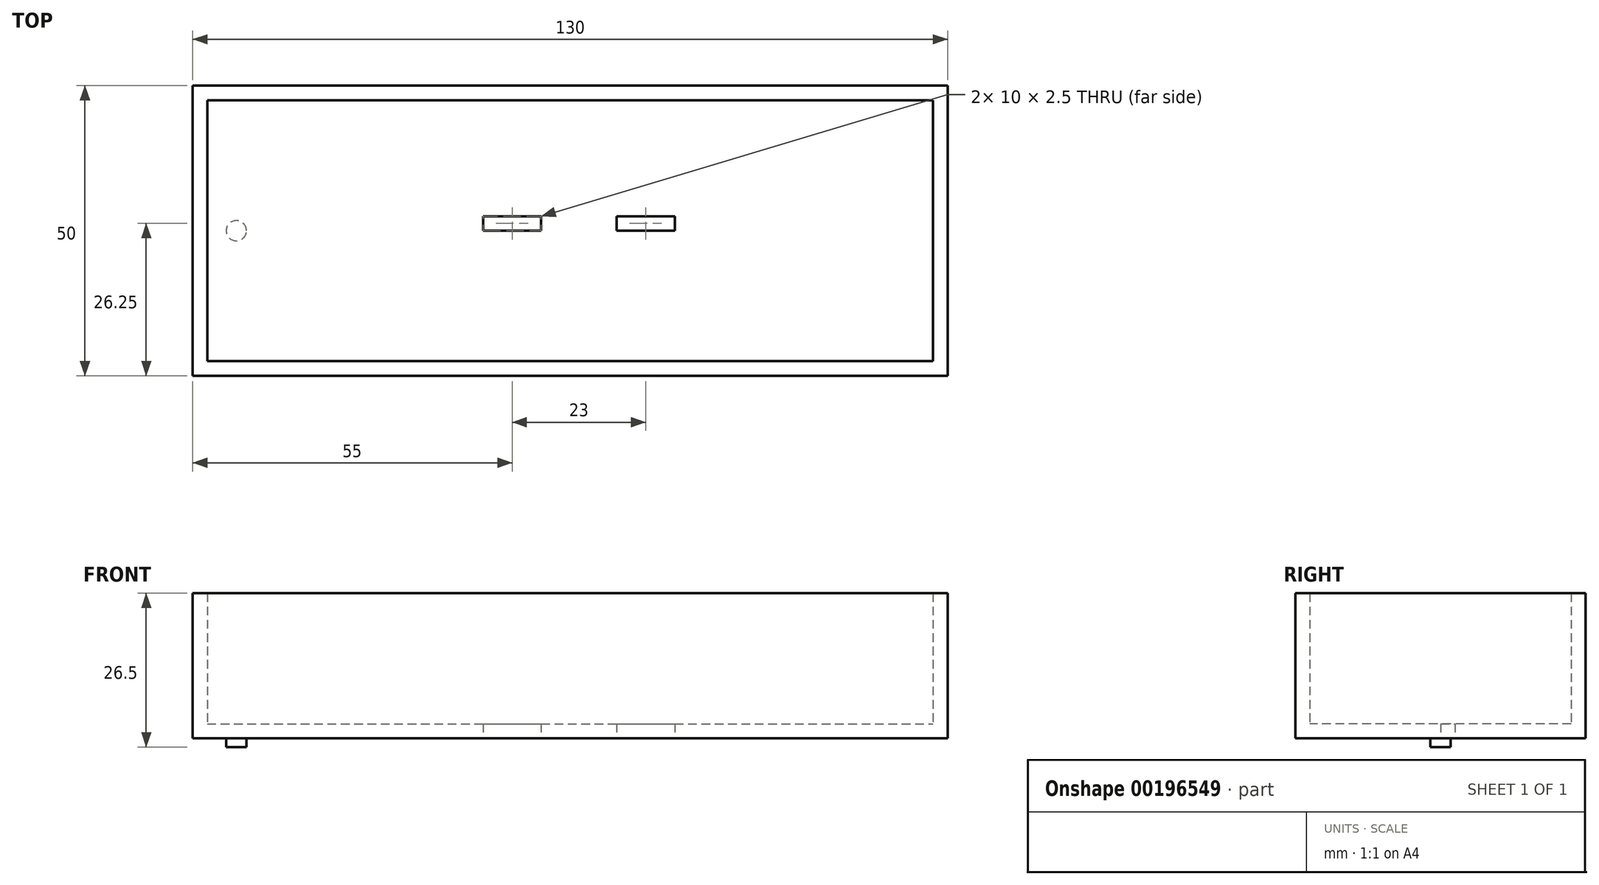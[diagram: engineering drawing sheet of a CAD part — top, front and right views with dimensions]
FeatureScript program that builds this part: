
annotation { "Feature Type Name" : "Feature", "Feature Type Description" : "" }
export const myFeature = defineFeature(function(context is Context, id is Id, definition is map)
    precondition{}
    {
        {
            var Q0;
            Q0=qCreatedBy(makeId("Top.planeOp"),FACE);
            var sketch = newSketch(context, id + "F0", { "sketchPlane" : qUnion([Q0])});
            skLineSegment(sketch, "E0.bottom", {"start": v(0, 25) * mm, "end": v(130, 25) * mm});
            skLineSegment(sketch, "E0.top", {"start": v(0, -25) * mm, "end": v(130, -25) * mm});
            skLineSegment(sketch, "E0.left", {"start": v(0, 25) * mm, "end": v(0, -25) * mm});
            skLineSegment(sketch, "E0.right", {"start": v(130, 25) * mm, "end": v(130, -25) * mm});
            skSolve(sketch);
        }
        {
            var Q0;
            Q0 = qSketchRegion(id + "F0", true);
            extrude(context, id + "F1", {"entities" : qUnion([Q0]), "depth" : 25 * mm});
        }
        {
            var Q0;
            Q0=makeQuery(id+"F1.opExtrude","CAP_FACE",FACE,{"disambiguationData":[OSD([sQuery(id+"F0.wireOp",EDGE,"E0.bottom"),sQuery(id+"F0.wireOp",EDGE,"E0.top"),sQuery(id+"F0.wireOp",EDGE,"E0.left"),sQuery(id+"F0.wireOp",EDGE,"E0.right")])],"isStart":false});
            shell(context, id + "F2", {"entities" : qUnion([Q0]), "thickness" : 2.5 * mm});
        }
        {
            var Q0;
            Q0=makeQuery(id+"F1.opExtrude","CAP_FACE",FACE,{"disambiguationData":[OSD([sQuery(id+"F0.wireOp",EDGE,"E0.bottom"),sQuery(id+"F0.wireOp",EDGE,"E0.top"),sQuery(id+"F0.wireOp",EDGE,"E0.left"),sQuery(id+"F0.wireOp",EDGE,"E0.right")])],"isStart":true});
            var sketch = newSketch(context, id + "F3", { "sketchPlane" : qUnion([Q0])});
            skCircle(sketch, "E1", {"center": v(7.5, 0) * mm, "radius": 1.75 * mm});
            skSolve(sketch);
        }
        {
            var Q0;
            Q0 = qSketchRegion(id + "F3", true);
            extrude(context, id + "F4", {"entities" : qUnion([Q0]), "operationType" : NewBodyOperationType.ADD, "depth" : 1.5 * mm});
        }
        {
            var Q0;
            Q0=makeQuery(id+"F1.opExtrude","CAP_FACE",FACE,{"disambiguationData":[OSD([sQuery(id+"F0.wireOp",EDGE,"E0.bottom"),sQuery(id+"F0.wireOp",EDGE,"E0.top"),sQuery(id+"F0.wireOp",EDGE,"E0.left"),sQuery(id+"F0.wireOp",EDGE,"E0.right")])],"isStart":true});
            var sketch = newSketch(context, id + "F5", { "sketchPlane" : qUnion([Q0])});
            skLineSegment(sketch, "E2.bottom", {"start": v(50, 0) * mm, "end": v(60, 0) * mm});
            skLineSegment(sketch, "E2.top", {"start": v(50, -2.5) * mm, "end": v(60, -2.5) * mm});
            skLineSegment(sketch, "E2.left", {"start": v(50, 0) * mm, "end": v(50, -2.5) * mm});
            skLineSegment(sketch, "E2.right", {"start": v(60, 0) * mm, "end": v(60, -2.5) * mm});
            skLineSegment(sketch, "E3.bottom", {"start": v(73, 0) * mm, "end": v(83, 0) * mm});
            skLineSegment(sketch, "E3.top", {"start": v(73, -2.5) * mm, "end": v(83, -2.5) * mm});
            skLineSegment(sketch, "E3.left", {"start": v(73, 0) * mm, "end": v(73, -2.5) * mm});
            skLineSegment(sketch, "E3.right", {"start": v(83, 0) * mm, "end": v(83, -2.5) * mm});
            skSolve(sketch);
        }
        {
            var Q0;
            Q0 = qSketchRegion(id + "F5", true);
            extrude(context, id + "F6", {"entities" : qUnion([Q0]), "operationType" : NewBodyOperationType.REMOVE, "endBound" : BoundingType.UP_TO_NEXT, "oppositeDirection" : true, "depth" : 25 * mm});
        }
    });
